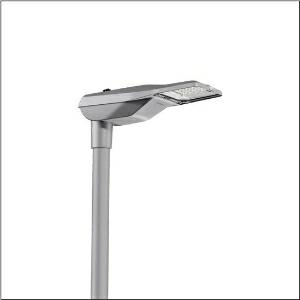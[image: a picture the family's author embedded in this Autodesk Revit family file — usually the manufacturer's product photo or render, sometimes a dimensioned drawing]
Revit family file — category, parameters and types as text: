
# Revit family: streetlight_sl_21_micro___stw1_0a_5xe1e33s08db_cbec
name_source: partatom
category: Lighting Fixtures
units: mm (PartAtom-declared; Revit-internal decimal feet)

## family parameters
Cut with Voids When Loaded = No
Host = Face
Light Source = No
Part Type = Normal
Room Calculation Point = No
Round Connector Dimension = Use Diameter
Shared = No

## types (1)
- --- (1 x LED, 5110 lm, 39.1 W, 3000K)
    Apparent Load = 39 VA
    CIE Flux Codes = 38 75 98 100 100
    Color Rendering = 70
    Color Temperature = 3000K
    Default Elevation = 1800 mm
    Description = Streetlight SL 21 micro, mast luminaire, primary light control with lens, of PMMA, primary optical cover: cover, of toughened safety glass, transparent, light distribution: STW1.0a, light emission: direct distribution, primary light characteristic: asymmetric, installation type: side-entry, post-top, LED, High Power LED, rated luminous flux: 5.110lm, luminous efficacy: 131lm/W, light colour: 730, colour temperature: 3000K, control gear: D4i, control: flexible luminous flux parameterisation, time-dependent luminous flux control, constant luminous flux control, overheat protection, pre-setting: logarithmic dimming characteristic, mains connection: 220..240V, AC, 50/60Hz, start of lifetime: 39W, end of service life: 41W, reduction: 18W, luminaire housing, of diecast aluminium, powder-coated, Siteco® metallic grey (DB 702S), corrosivity category C5 mid according to DIN EN ISO 12944, please order mast flange separately, inclination adjustable: 0°, 5°, 10°, 15°, sealing non-destructively replaceable, multi-level sealing system, length: 528mm, width: 235mm, height: 110mm, mast flange for spigot size: 42mm (side-entry): 5XC10008XM4, 60/48mm (side-entry/post-top): 5XC10108XM2, 76/60mm (side-entry/post-top): 5XC10108XM1, Smart Interface above, protection rating (complete): IP66, insulation class (complete): insulation class II (safety insulation), certification: CE, ENEC, ENEC+, VDE, impact resistance: IK10, permissible operating ambient temperature for outdoor applications: -40..+50°C, standard-compliant lighting for roads and squares, packaging unit: 1 piece

Light Distribution: STW1.0a
    Height = 110 mm
    Lamp = 1 x LED
    Lamp Light Flux = 5110 lm
    Lamp Power = 39.1 W
    Lamp count = 1
    Length = 528 mm
    Luminous efficacy = 131 lm/W
    Manufacturer = Siteco
    ModVariant = No
    Model = 5XE1E33S08DB
    Number of Poles = 1
    OnlyDefault = Yes
    Power Factor = 1
    Product Name = Streetlight SL 21 micro | STW1.0a
    Product group = mast luminaire | pylon top
    ProductGroupID = 6100
    Protection Class = Protection class II
    Protection Degree = IP 66
    RLX_Detail_Level = 1
    RLX_Emergency_Light_Flux = 0 lm
    RLX_Emergency_Type = 0
    RLX_Emergency_Type_DB = No
    RlxData = <blob elided: 98125 chars, md5=aced9f4d>
    Socket = socket
    Standby Power = 0 W
    System Light Flux = 5110 lm
    System Power = 39 W
    Type Comments = factory setting: luminous flux: 100 % | dim-lin: 254 | 765 mA
    Type Image = l_1277292.jpg
    URL = http://relux.com
    VarID = @adj_176827
    Voltage = 0 V
    Weight = 0.00 kg
    Width = 235 mm

## geometry (parser evidence)
native form markers: Blend x4, Sweep x9
no freeform markers — native parametric forms only
